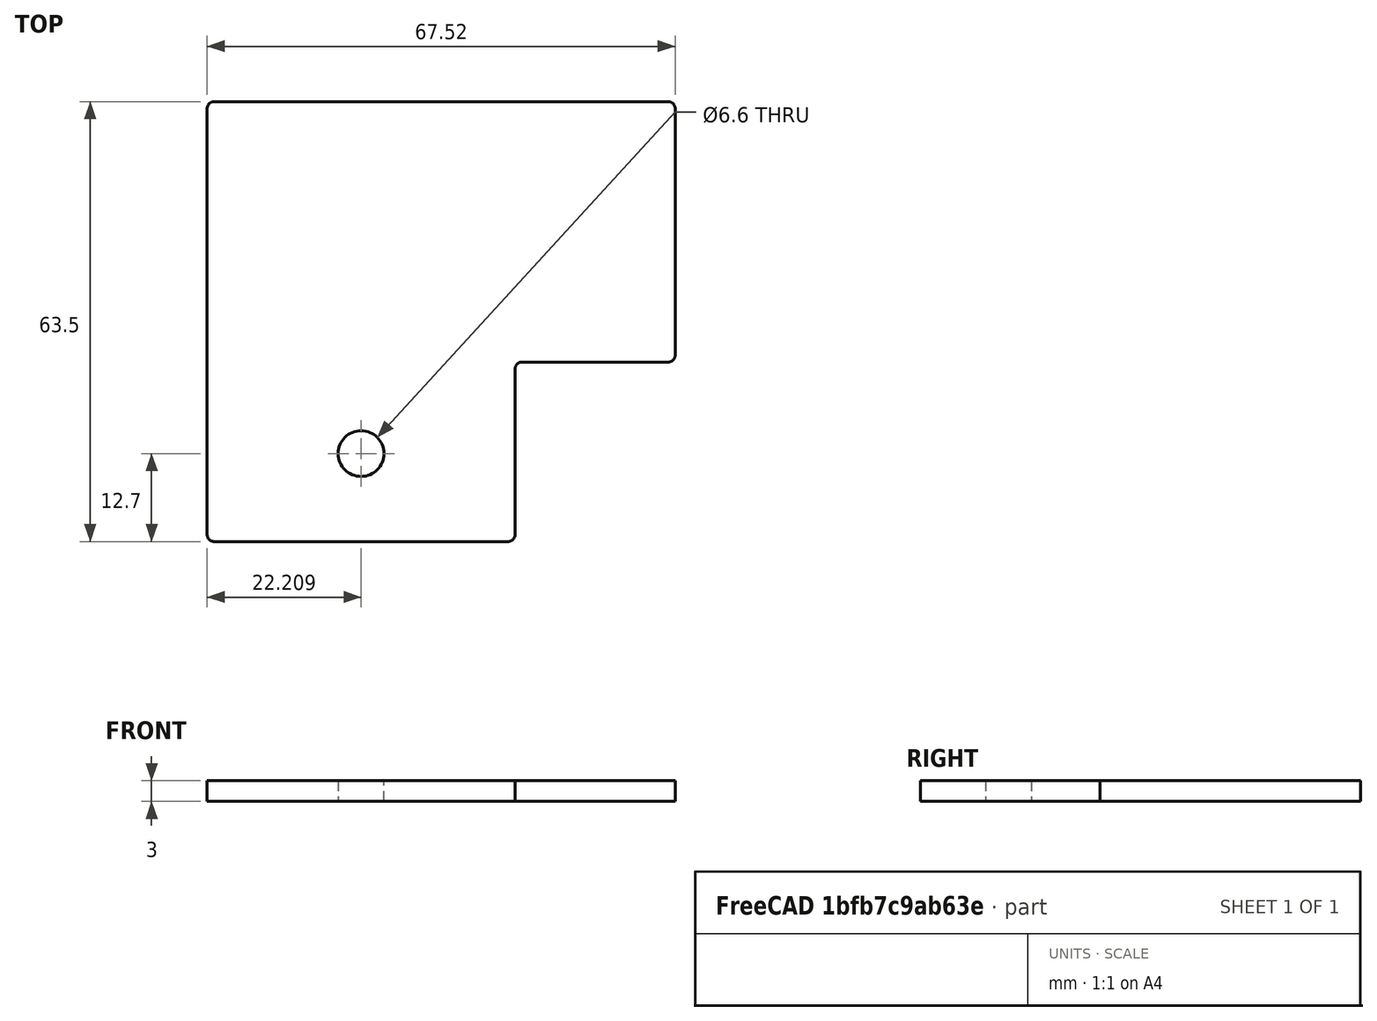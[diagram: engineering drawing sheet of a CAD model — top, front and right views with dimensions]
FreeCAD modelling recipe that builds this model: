
FCSTD DOCUMENT  (FreeCAD 0.20R29603 (Git))
Label: right_wall_back_test_rig
License: All rights reserved
LicenseURL: http://en.wikipedia.org/wiki/All_rights_reserved
objects: Sketcher::SketchObject×2, Spreadsheet::Sheet×1, PartDesign::Pad×1, PartDesign::Body×1, Part::Part2DObjectPython×1
note: 6 computed .brp shape members not serialized (recipe doc carries the construction recipe); baked Part::Feature solids carry a one-line shape summary decoded from their .brp

FEATURE [Spreadsheet::Sheet] Spreadsheet
  cells = A2=Parameters; A3=BeamLength; B3(BeamLength)==7.8125in; A4=BracketLength; B4(BracketLength)==108.6mm; A5=DistanceLeftBracketEdgeToDoor; B5(DistanceLeftBracketEdgeToDoor)==82.4999mm; A6=DistanceRightBracketEdgeToDoor; B6(DistanceRightBracketEdgeToDoor)==23.6001mm; A7=LengthMargin; B7(LengthMargin)==0.5mm; A8=LengthLeftBracketEdgeToDoorGap; B8(LengthLeftBracketEdgeToDoorGap)==DistanceLeftBracketEdgeToDoor - LengthMargin; A9=LengthRightBracketEdgeToDoorGap; B9(LengthRightBracketEdgeToDoorGap)==DistanceRightBracketEdgeToDoor - LengthMargin; A10=LengthDoorGap; B10(LengthDoorGap)==BracketLength - LengthLeftBracketEdgeToDoorGap - LengthRightBracketEdgeToDoorGap; A11=BeamLengthMinusBracketLength; B11(BeamLengthMinusBracketLength)==BeamLength - BracketLength; A13=DistanceBackToDoor; B13(DistanceBackToDoor)==0.5 * BeamLengthMinusBracketLength + LengthRightBracketEdgeToDoorGap; A14=DistanceBackToBracket; B14(DistanceBackToBracket)==0.5 * BeamLengthMinusBracketLength; A15=LengthBackToDoor; B15(LengthBackToDoor)==DistanceBackToDoor - LengthMargin; A16=LengthBackToBracket; B16(LengthBackToBracket)==DistanceBackToBracket - LengthMargin; A17=Height; B17(Height)==2.5in; A18=Thickness; B18(Thickness)==3mm; A19=CutoutMargin; B19(CutoutMargin)==0.5mm; A20=CutoutHeight; B20(CutoutHeight)==1in + CutoutMargin; A21=FilletRadius; B21(FilletRadius)==1mm; A22=MountHoleDiameter; B22(MountHoleDiameter)==0.26in; A23=MountHoleDistanceFromBottom; B23(MountHoleDistanceFromBottom)==0.5in
FEATURE [Sketcher::SketchObject] Sketch
  FullyConstrained = true
  MapMode = 5
  Support = -> [XY_Plane]
  expr: Constraints[14] = Spreadsheet.FilletRadius
  expr: Constraints[20] = Spreadsheet.Height
  expr: Constraints[44] = Spreadsheet.MountHoleDistanceFromBottom
  expr: Constraints[45] = Spreadsheet.MountHoleDiameter
  expr: Constraints[7] = Spreadsheet.LengthBackToDoor
  expr: Constraints[8] = Spreadsheet.LengthBackToBracket
  expr: Constraints[9] = Spreadsheet.CutoutHeight
  sketch-geometry (21):
    g0: LineSegment StartX=0 StartY=62.5 StartZ=0 EndX=0 EndY=1 EndZ=0
    g1: LineSegment StartX=1 StartY=0 StartZ=0 EndX=43.4188 EndY=0 EndZ=0
    g2: LineSegment StartX=44.4187 StartY=1 StartZ=0 EndX=44.4187 EndY=24.9 EndZ=0
    g3: LineSegment StartX=45.4187 StartY=25.9 StartZ=0 EndX=66.5189 EndY=25.9 EndZ=0
    g4: LineSegment StartX=67.5189 StartY=26.9 StartZ=0 EndX=67.5189 EndY=62.5 EndZ=0
    g5: LineSegment StartX=66.5189 StartY=63.5 StartZ=0 EndX=1 EndY=63.5 EndZ=0
    g6: ArcOfCircle CenterX=1 CenterY=62.5 CenterZ=0 NormalX=0 NormalY=0 NormalZ=1 AngleXU=0 Radius=1 StartAngle=1.5708 EndAngle=3.14159
    g7: GeomPoint X=0 Y=63.5 Z=0
    g8: ArcOfCircle CenterX=1 CenterY=1 CenterZ=0 NormalX=0 NormalY=0 NormalZ=1 AngleXU=0 Radius=1 StartAngle=3.14159 EndAngle=4.71239
    g9: GeomPoint X=0 Y=0 Z=0
    g10: ArcOfCircle CenterX=43.4188 CenterY=1 CenterZ=0 NormalX=0 NormalY=0 NormalZ=1 AngleXU=0 Radius=1 StartAngle=4.71239 EndAngle=6.28319
    g11: GeomPoint X=44.4188 Y=0 Z=0
    g12: ArcOfCircle CenterX=45.4187 CenterY=24.9 CenterZ=0 NormalX=0 NormalY=0 NormalZ=1 AngleXU=0 Radius=1 StartAngle=1.5708 EndAngle=3.14159
    g13: GeomPoint X=44.4188 Y=25.9 Z=0
    g14: ArcOfCircle CenterX=66.5189 CenterY=26.9 CenterZ=0 NormalX=0 NormalY=0 NormalZ=1 AngleXU=0 Radius=1 StartAngle=4.71239 EndAngle=6.28319
    g15: GeomPoint X=67.5189 Y=25.9 Z=0
    g16: ArcOfCircle CenterX=66.5189 CenterY=62.5 CenterZ=0 NormalX=0 NormalY=0 NormalZ=1 AngleXU=0 Radius=1 StartAngle=1.2e-15 EndAngle=1.5708
    g17: GeomPoint X=67.5189 Y=63.5 Z=0
    g18: GeomPoint X=22.2094 Y=0 Z=0
    g19: LineSegment StartX=22.2094 StartY=0 StartZ=0 EndX=22.2094 EndY=12.7 EndZ=0
    g20: Circle CenterX=22.2094 CenterY=12.7 CenterZ=0 NormalX=0 NormalY=0 NormalZ=1 AngleXU=0 Radius=3.302
  constraints (47):
    c: Vertical(g0)
    c: Horizontal(g1)
    c: Vertical(g2)
    c: Horizontal(g3)
    c: Vertical(g4)
    c: Horizontal(g5)
    c: Coincident(g-1,g9)
    c: DistanceX(g7,g17) = 67.5189
    c: DistanceX(g9,g11) = 44.4188
    c: DistanceY(g11,g13) = 25.9
    c: PointOnObject(g7,g0)
    c: PointOnObject(g7,g5)
    c: Tangent(g0,g6) = -1.5708
    c: Tangent(g5,g6) = -1.5708
    c: Radius(g6) = 1
    c: PointOnObject(g9,g0)
    c: PointOnObject(g9,g1)
    c: Tangent(g0,g8) = -1.5708
    c: Tangent(g1,g8) = -1.5708
    c: Equal(g8,g6)
    c: DistanceY(g1,g5) = 63.5
    c: PointOnObject(g11,g1)
    c: PointOnObject(g11,g2)
    c: Tangent(g1,g10) = -1.5708
    c: Tangent(g2,g10) = -1.5708
    c: Equal(g10,g8)
    c: PointOnObject(g13,g2)
    c: PointOnObject(g13,g3)
    c: Tangent(g2,g12) = 1.5708
    c: Tangent(g3,g12) = 1.5708
    c: Equal(g12,g10)
    c: PointOnObject(g15,g3)
    c: PointOnObject(g15,g4)
    c: Tangent(g3,g14) = -1.5708
    c: Tangent(g4,g14) = -1.5708
    c: Equal(g14,g12)
    c: PointOnObject(g17,g5)
    c: PointOnObject(g17,g4)
    c: Tangent(g5,g16) = -1.5708
    c: Tangent(g4,g16) = -1.5708
    c: Equal(g16,g14)
    c: Symmetric(g1,g1,g18)
    c: Coincident(g19,g18)
    c: Vertical(g19)
    c: DistanceY(g19,g19) = 12.7
    c: Diameter(g20) = 6.604
    c: Coincident(g20,g19)
FEATURE [PartDesign::Pad] Pad
  Direction = (0,0,1)
  Length = 3
  Length2 = 10
  Profile = -> Sketch
  ReferenceAxis = -> Sketch [N_Axis]
  Type = 0
  expr: Length = Spreadsheet.Thickness
FEATURE [PartDesign::Body] Body
  Group = -> [Sketch,Pad]
  Origin = -> Origin
  Tip = -> Pad
FEATURE [Part::Part2DObjectPython] Shape2DView  # Draft 2D object (typed FeaturePython)
  AutoUpdate = true
  Base = -> Pad
  Clip = false
  FuseArch = false
  HiddenLines = false
  InPlace = true
  OnlySolids = false
  Projection = (0,0,1)
  ProjectionMode = 0
  SegmentLength = 0.05
  Tessellation = false
  VisibleOnly = false
FEATURE [Sketcher::SketchObject] Sketch001
  FullyConstrained = false
  sketch-geometry (13):
    g0: LineSegment StartX=45.4187 StartY=25.9 StartZ=0 EndX=66.5189 EndY=25.9 EndZ=0
    g1: ArcOfCircle CenterX=66.5189 CenterY=26.9 CenterZ=0 NormalX=0 NormalY=0 NormalZ=1 AngleXU=0 Radius=1 StartAngle=4.71239 EndAngle=6.28319
    g2: LineSegment StartX=67.5189 StartY=26.9 StartZ=0 EndX=67.5189 EndY=62.5 EndZ=0
    g3: ArcOfCircle CenterX=66.5189 CenterY=62.5 CenterZ=0 NormalX=0 NormalY=0 NormalZ=1 AngleXU=0 Radius=1 StartAngle=1e-15 EndAngle=1.5708
    g4: LineSegment StartX=66.5189 StartY=63.5 StartZ=0 EndX=1 EndY=63.5 EndZ=0
    g5: ArcOfCircle CenterX=1 CenterY=62.5 CenterZ=0 NormalX=0 NormalY=0 NormalZ=1 AngleXU=0 Radius=1 StartAngle=1.5708 EndAngle=3.14159
    g6: LineSegment StartX=0 StartY=62.5 StartZ=0 EndX=0 EndY=1 EndZ=0
    g7: ArcOfCircle CenterX=1 CenterY=1 CenterZ=0 NormalX=0 NormalY=0 NormalZ=1 AngleXU=0 Radius=1 StartAngle=3.14159 EndAngle=4.71239
    g8: LineSegment StartX=1 StartY=0 StartZ=0 EndX=43.4188 EndY=0 EndZ=0
    g9: ArcOfCircle CenterX=43.4188 CenterY=1 CenterZ=0 NormalX=0 NormalY=0 NormalZ=1 AngleXU=0 Radius=1 StartAngle=4.71239 EndAngle=6.28319
    g10: LineSegment StartX=44.4187 StartY=1 StartZ=0 EndX=44.4187 EndY=24.9 EndZ=0
    g11: ArcOfCircle CenterX=45.4187 CenterY=24.9 CenterZ=0 NormalX=0 NormalY=0 NormalZ=1 AngleXU=0 Radius=1 StartAngle=1.5708 EndAngle=3.14159
    g12: Circle CenterX=22.2094 CenterY=12.7 CenterZ=0 NormalX=0 NormalY=0 NormalZ=1 AngleXU=0 Radius=3.302
